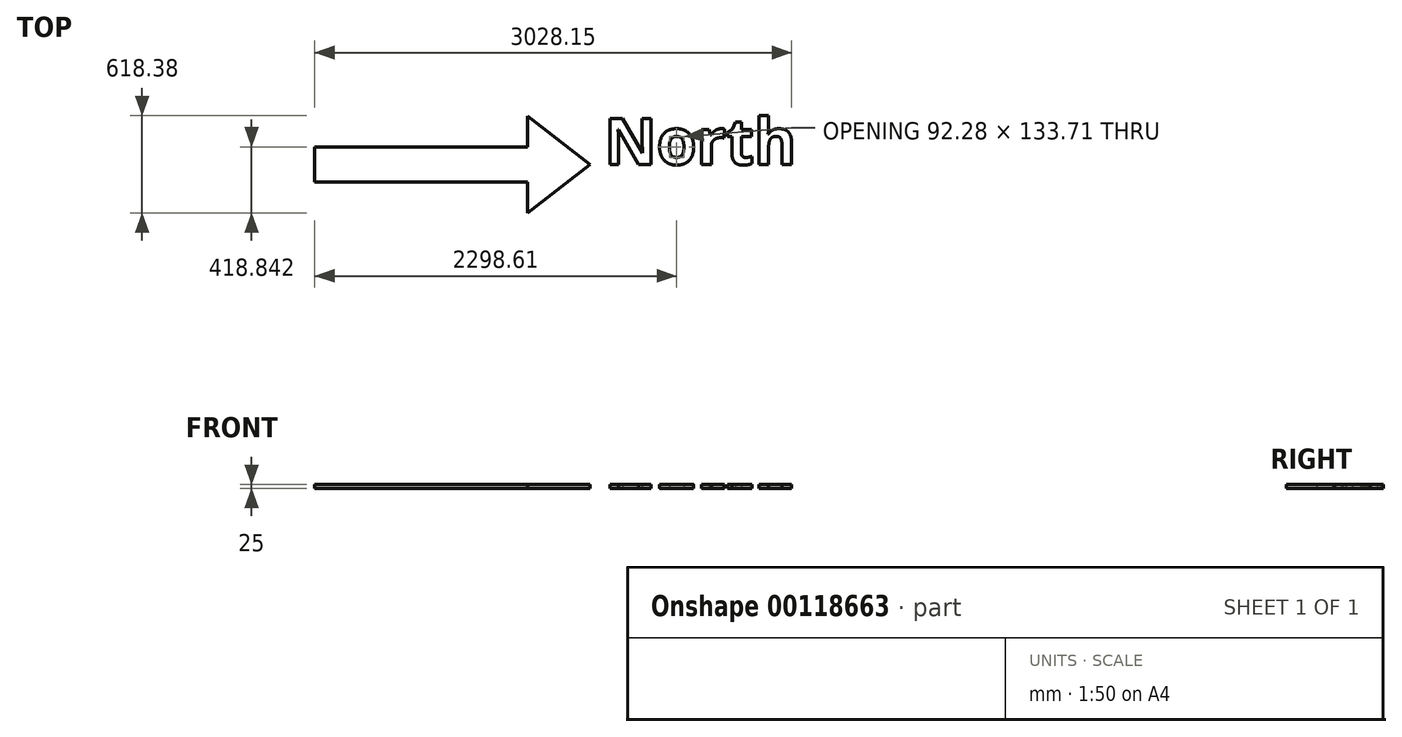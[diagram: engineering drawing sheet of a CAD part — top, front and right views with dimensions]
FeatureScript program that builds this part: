
annotation { "Feature Type Name" : "Feature", "Feature Type Description" : "" }
export const myFeature = defineFeature(function(context is Context, id is Id, definition is map)
    precondition{}
    {
        {
            var Q0;
            Q0=qCreatedBy(makeId("Top.planeOp"),FACE);
            var sketch = newSketch(context, id + "F0", { "sketchPlane" : qUnion([Q0])});
            skText(sketch, "E0", { "text": "North", "fontName": "OpenSans-Bold.ttf"});
            skLineSegment(sketch, "E1", {"start": v(-747.59, 0) * mm, "end": v(-747.59, 112.06) * mm});
            skLineSegment(sketch, "E2", {"start": v(-747.59, 112.06) * mm, "end": v(604.62, 112.06) * mm});
            skLineSegment(sketch, "E3", {"start": v(604.62, 112.06) * mm, "end": v(604.62, 306.97) * mm});
            skLineSegment(sketch, "E4", {"start": v(604.62, 306.97) * mm, "end": v(1002.2, 0) * mm});
            skLineSegment(sketch, "E5", {"start": v(1002.2, 0) * mm, "end": v(-747.59, 0) * mm});
            const initialGuessF0  = {"E0": [1.09108, 0, 1, 0, 0.29508]};
            skSetInitialGuess(sketch, initialGuessF0);
            skSolve(sketch);
        }
        {
            var Q0;
            Q0=makeQuery(id+"F0.imprint","IMPRINT",FACE,{"disambiguationData":[TD([[makeQuery(id+"F0.imprint","IMPRINT",EDGE,{"derivedFrom":sQuery(id+"F0.wireOp",EDGE,"E1")}),-1.0]])]});
            extrude(context, id + "F1", {"entities" : qUnion([Q0]), "depth" : 25 * mm});
        }
        {
            var Q0;
            Q0=makeQuery(id+"F1.opExtrude","SWEPT_BODY",BODY,{"disambiguationData":[OSD([sQuery(id+"F0.wireOp",EDGE,"E1"),sQuery(id+"F0.wireOp",EDGE,"E2"),sQuery(id+"F0.wireOp",EDGE,"E3"),sQuery(id+"F0.wireOp",EDGE,"E4"),sQuery(id+"F0.wireOp",EDGE,"E5")])]});
            var Q1;
            Q1=qCreatedBy(makeId("Front.planeOp"),FACE);
            mirror(context, id + "F2", {"operationType" : NewBodyOperationType.ADD, "entities" : qUnion([Q0]), "mirrorPlane" : qUnion([Q1])});
        }
        {
            var Q0;
            Q0=makeQuery(id+"F0.imprint","IMPRINT",FACE,{"disambiguationData":[TD([[makeQuery(id+"F0.imprint","IMPRINT",EDGE,{"derivedFrom":sQuery(id+"F0.wireOp",EDGE,"E0.sketch_text.stroke-14")}),-1.0]])]});
            var Q1;
            Q1=makeQuery(id+"F0.imprint","IMPRINT",FACE,{"disambiguationData":[TD([[makeQuery(id+"F0.imprint","IMPRINT",EDGE,{"derivedFrom":sQuery(id+"F0.wireOp",EDGE,"E0.sketch_text.stroke-32")}),-1.0]])]});
            var Q2;
            Q2=makeQuery(id+"F0.imprint","IMPRINT",FACE,{"disambiguationData":[TD([[makeQuery(id+"F0.imprint","IMPRINT",EDGE,{"derivedFrom":sQuery(id+"F0.wireOp",EDGE,"E0.sketch_text.stroke-45")}),-1.0]])]});
            var Q3;
            Q3=makeQuery(id+"F0.imprint","IMPRINT",FACE,{"disambiguationData":[TD([[makeQuery(id+"F0.imprint","IMPRINT",EDGE,{"derivedFrom":sQuery(id+"F0.wireOp",EDGE,"E0.sketch_text.stroke-63")}),-1.0]])]});
            var Q4;
            Q4=makeQuery(id+"F0.imprint","IMPRINT",FACE,{"disambiguationData":[TD([[makeQuery(id+"F0.imprint","IMPRINT",EDGE,{"derivedFrom":sQuery(id+"F0.wireOp",EDGE,"E0.sketch_text.stroke-0")}),-1.0]])]});
            extrude(context, id + "F3", {"entities" : qUnion([Q0, Q1, Q2, Q3, Q4]), "depth" : 25 * mm});
        }
    });
